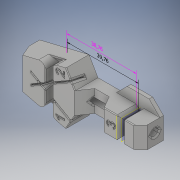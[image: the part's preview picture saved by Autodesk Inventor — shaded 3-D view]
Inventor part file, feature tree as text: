
AUTODESK INVENTOR PART (.ipt)
format: ipt  version: 2019.4 (Build 234330000, 330)  size: 2,167,808 bytes
history: native  units: in
note: dims shown in document units (in); Inventor stores cm internally (conversion verified against a paired STEP export)
features: extrude x5, sketch x5, other x3, plane x2, fillet x2, chamfer x2, projected_geometry x2
ambient origin geometry x8: Origin, YZ Plane, XZ Plane, XY Plane, X Axis, Y Axis, Z Axis, Center Point
bodies: Solid1 (feature_tree), Body3 (feature_tree)
feature tree (21):
  other  "Annotations"
  plane  "Work Plane1"
  extrude  "Extrusion1"  Depth=0.0394in TaperAngle=0.0deg
  plane  "Work Plane2"
  extrude  "Extrusion2"  Depth=0.0787in TaperAngle=0.0deg
  extrude  "Extrusion3"  Depth=0.0197in
  fillet  "Fillet1"  Radius=0.0197in
  chamfer  "Chamfer1"  Distance=0.0394in
  chamfer  "Chamfer2"  Distance=0.0236in
  fillet  "Fillet2"  [1 undecoded]
  extrude  "Extrusion4"  [1 undecoded]
  extrude  "Extrusion5"  [1 undecoded]
  sketch  "Sketch1"  dims[d3=-0.0394in d4=0.0394in d5=0.0in]
  sketch  "Sketch2"  dims[d6=-0.0394in d7=0.0787in d8=0.0in]
  sketch  "Sketch3"  dims[d9=0.0787in d10=0.0in d11=0.0197in]
  sketch  "Sketch4"  dims[d12=0.0787in d13=0.0787in d14=45.0deg]
  sketch  "Sketch5"  dims[d15=0.0787in d16=0.0787in d17=45.0deg d18=0.0197in d19=0.0394in d20=0.0in d21=0.0236in d22=0.0in d0=0.2309in d1=0.1141in d2=1.526in d23=0.2012in d24=0.0906in d25=1.5654in]
  projected_geometry  "Project Cut Edges1"
  projected_geometry  "Project Cut Edges2"
  other  "Linear Dimension 1"
  other  "Linear Dimension 2"
note: 3 required parameter values undecoded (feature->parameter linkage not recoverable at this tier; creation-order binding heuristic only, values carry confidence <= 0.55)
